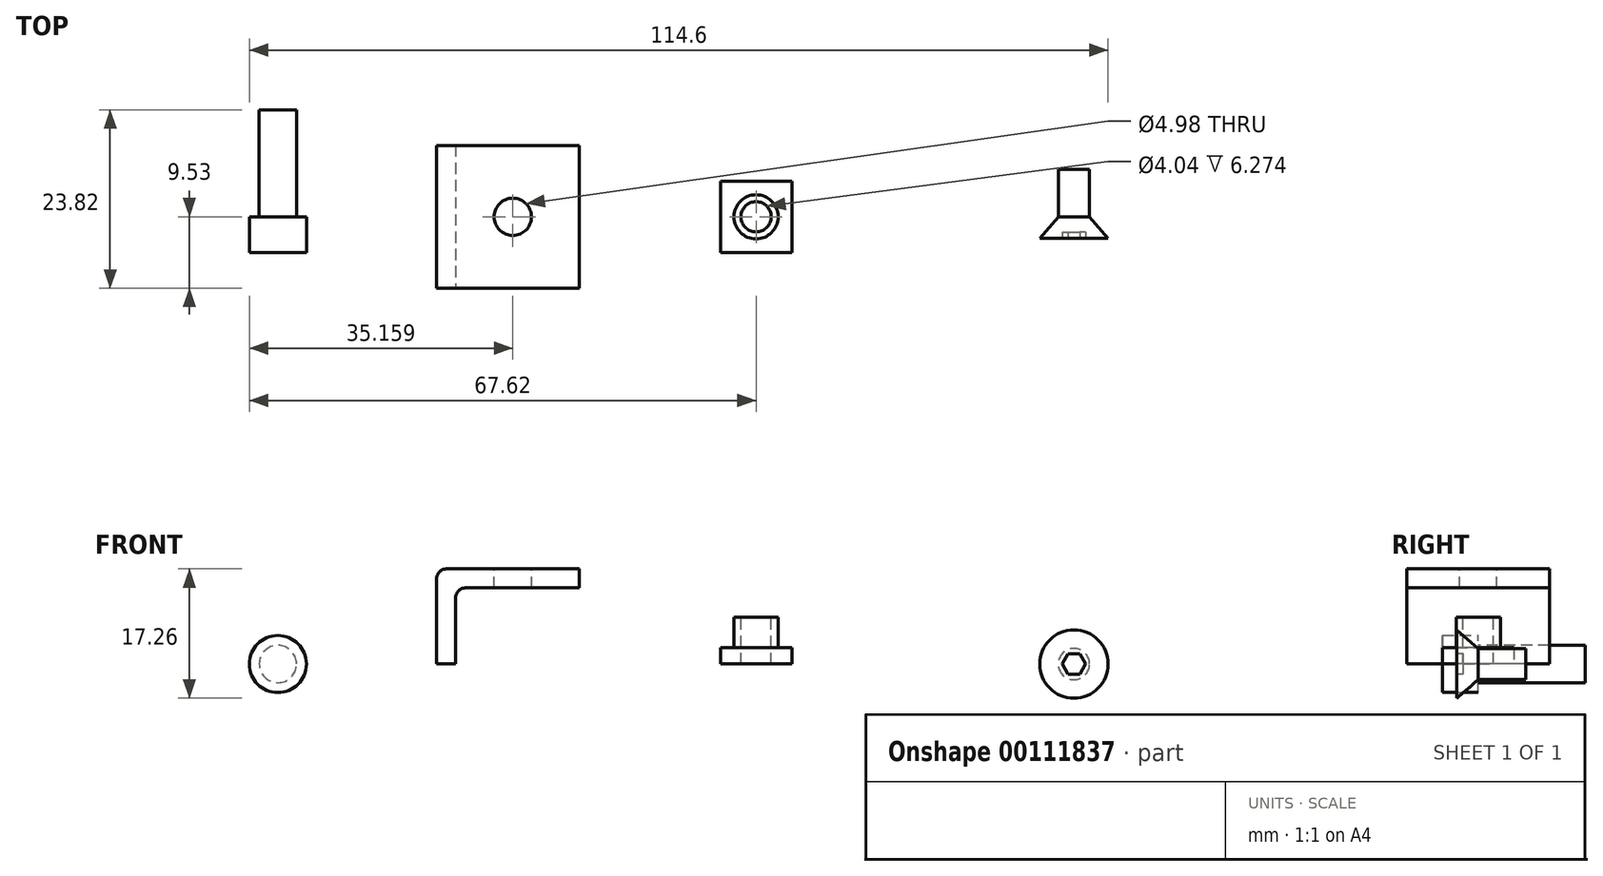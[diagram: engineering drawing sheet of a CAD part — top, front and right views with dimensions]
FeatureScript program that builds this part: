
annotation { "Feature Type Name" : "Feature", "Feature Type Description" : "" }
export const myFeature = defineFeature(function(context is Context, id is Id, definition is map)
    precondition{}
    {
        {
            var Q0;
            Q0=qCreatedBy(makeId("Top.planeOp"),FACE);
            var sketch = newSketch(context, id + "F0", { "sketchPlane" : qUnion([Q0])});
            skLineSegment(sketch, "E0.bottom", {"start": v(4.76, 4.76) * mm, "end": v(-4.76, 4.76) * mm});
            skLineSegment(sketch, "E0.top", {"start": v(4.76, -4.76) * mm, "end": v(-4.76, -4.76) * mm});
            skLineSegment(sketch, "E0.left", {"start": v(4.76, 4.76) * mm, "end": v(4.76, -4.76) * mm});
            skLineSegment(sketch, "E0.right", {"start": v(-4.76, 4.76) * mm, "end": v(-4.76, -4.76) * mm});
            skPoint(sketch, "E0.middle", {"position": v(0, 0) * mm});
            skSolve(sketch);
        }
        {
            var Q0;
            Q0=qSketchRegion(id+"F0",true);
            extrude(context, id + "F1", {"entities" : qUnion([Q0]), "depth" : 2.2 * mm});
        }
        {
            var Q0;
            Q0=makeQuery(id+"F1.opExtrude","CAP_FACE",FACE,{"disambiguationData":[OSD([sQuery(id+"F0.wireOp",EDGE,"E0.bottom"),sQuery(id+"F0.wireOp",EDGE,"E0.top"),sQuery(id+"F0.wireOp",EDGE,"E0.left"),sQuery(id+"F0.wireOp",EDGE,"E0.right")])],"isStart":false});
            var sketch = newSketch(context, id + "F2", { "sketchPlane" : qUnion([Q0])});
            skCircle(sketch, "E1", {"center": v(0, 0) * mm, "radius": 2.95 * mm});
            skSolve(sketch);
        }
        {
            var Q0;
            Q0=qSketchRegion(id+"F2",true);
            extrude(context, id + "F3", {"entities" : qUnion([Q0]), "operationType" : NewBodyOperationType.ADD, "depth" : 4.06 * mm});
        }
        {
            var Q0;
            Q0=makeQuery(id+"F3.opExtrude","CAP_FACE",FACE,{"disambiguationData":[OSD([sQuery(id+"F2.wireOp",EDGE,"E1")])],"isStart":false});
            var sketch = newSketch(context, id + "F4", { "sketchPlane" : qUnion([Q0])});
            skPoint(sketch, "E2", {"position": v(0, 0) * mm});
            skSolve(sketch);
        }
        {
            var Q0;
            Q0=sQuery(id+"F4.wireOp",VERTEX,"E2");
            var Q1;
            Q1=makeQuery(id+"F1.opExtrude","SWEPT_BODY",BODY,{"disambiguationData":[OSD([sQuery(id+"F0.wireOp",EDGE,"E0.bottom"),sQuery(id+"F0.wireOp",EDGE,"E0.top"),sQuery(id+"F0.wireOp",EDGE,"E0.left"),sQuery(id+"F0.wireOp",EDGE,"E0.right")])]});
            hole(context, id + "F5", {"style" : HoleStyle.SIMPLE, "holeDiameter" : 4.04 * mm, "endStyle" : HoleEndStyle.THROUGH, "locations" : qUnion([Q0]), "scope" : qUnion([Q1])});
        }
        {
            var Q0;
            Q0=qCreatedBy(makeId("Front.planeOp"),FACE);
            var sketch = newSketch(context, id + "F6", { "sketchPlane" : qUnion([Q0])});
            skLineSegment(sketch, "E3.bottom", {"start": v(-42.62, 0) * mm, "end": v(-23.57, 0) * mm});
            skLineSegment(sketch, "E3.top", {"start": v(-42.62, 12.7) * mm, "end": v(-23.57, 12.7) * mm});
            skLineSegment(sketch, "E3.left", {"start": v(-42.62, 0) * mm, "end": v(-42.62, 12.7) * mm});
            skLineSegment(sketch, "E3.right", {"start": v(-23.57, 0) * mm, "end": v(-23.57, 12.7) * mm});
            skSolve(sketch);
        }
        {
            var Q0;
            Q0=qSketchRegion(id+"F6",true);
            extrude(context, id + "F7", {"entities" : qUnion([Q0]), "depth" : 19.05 * mm, "symmetric" : true});
        }
        {
            var Q0;
            Q0=makeQuery(id+"F7.opExtrude","CAP_FACE",FACE,{"disambiguationData":[OSD([sQuery(id+"F6.wireOp",EDGE,"E3.bottom"),sQuery(id+"F6.wireOp",EDGE,"E3.top"),sQuery(id+"F6.wireOp",EDGE,"E3.left"),sQuery(id+"F6.wireOp",EDGE,"E3.right")])],"isStart":false});
            var sketch = newSketch(context, id + "F8", { "sketchPlane" : qUnion([Q0])});
            skLineSegment(sketch, "E4", {"start": v(-40.08, 0) * mm, "end": v(-40.08, 10.16) * mm});
            skLineSegment(sketch, "E5", {"start": v(-40.08, 10.16) * mm, "end": v(-23.57, 10.16) * mm});
            skLineSegment(sketch, "E6", {"start": v(-23.57, 10.16) * mm, "end": v(-23.57, 0) * mm});
            skLineSegment(sketch, "E7", {"start": v(-23.57, 0) * mm, "end": v(-40.08, 0) * mm});
            skSolve(sketch);
        }
        {
            var Q0;
            Q0=qSketchRegion(id+"F8",true);
            extrude(context, id + "F9", {"entities" : qUnion([Q0]), "operationType" : NewBodyOperationType.REMOVE, "endBound" : BoundingType.THROUGH_ALL, "oppositeDirection" : true, "depth" : 25.4 * mm});
        }
        {
            var Q0;
            Q0=makeQuery(id+"F7.opExtrude","SWEPT_EDGE",EDGE,{"disambiguationData":[OSD([sQuery(id+"F6.wireOp",EDGE,"E3.top"),sQuery(id+"F6.wireOp",EDGE,"E3.left")])]});
            var Q1;
            Q1=makeQuery(id+"F9.boolean.opBoolean","COPY",EDGE,{"derivedFrom":makeQuery(id+"F9.opExtrude","SWEPT_EDGE",EDGE,{"disambiguationData":[OSD([sQuery(id+"F8.wireOp",EDGE,"E4"),sQuery(id+"F8.wireOp",EDGE,"E5")])]})});
            fillet(context, id + "F10", {"entities" : qUnion([Q0, Q1]), "radius" : 1.27 * mm, "tangentPropagation" : true, "allowEdgeOverflow" : false});
        }
        {
            var Q0;
            Q0=makeQuery(id+"F7.opExtrude","SWEPT_FACE",FACE,{"disambiguationData":[OSD([sQuery(id+"F6.wireOp",EDGE,"E3.top")])]});
            var sketch = newSketch(context, id + "F11", { "sketchPlane" : qUnion([Q0])});
            skPoint(sketch, "E8", {"position": v(-32.46, 0) * mm});
            skLineSegment(sketch, "E9", {"start": v(-32.46, 9.52) * mm, "end": v(-32.46, 0) * mm, "construction": true});
            skLineSegment(sketch, "E10", {"start": v(-32.46, -9.52) * mm, "end": v(-32.46, 0) * mm, "construction": true});
            skLineSegment(sketch, "E11", {"start": v(-32.46, 0) * mm, "end": v(-23.57, 0) * mm, "construction": true});
            skLineSegment(sketch, "E12", {"start": v(-42.62, 0) * mm, "end": v(-32.46, 0) * mm, "construction": true});
            skSolve(sketch);
        }
        {
            var Q0;
            Q0=sQuery(id+"F11.wireOp",VERTEX,"E8");
            var Q1;
            Q1=makeQuery(id+"F7.opExtrude","SWEPT_BODY",BODY,{"disambiguationData":[OSD([sQuery(id+"F6.wireOp",EDGE,"E3.bottom"),sQuery(id+"F6.wireOp",EDGE,"E3.top"),sQuery(id+"F6.wireOp",EDGE,"E3.left"),sQuery(id+"F6.wireOp",EDGE,"E3.right")])]});
            hole(context, id + "F12", {"style" : HoleStyle.SIMPLE, "holeDiameter" : 4.98 * mm, "endStyle" : HoleEndStyle.THROUGH, "locations" : qUnion([Q0]), "scope" : qUnion([Q1])});
        }
        {
            var Q0;
            Q0=qCreatedBy(makeId("Front.planeOp"),FACE);
            var sketch = newSketch(context, id + "F13", { "sketchPlane" : qUnion([Q0])});
            skCircle(sketch, "E13", {"center": v(-63.81, 0) * mm, "radius": 3.81 * mm});
            skSolve(sketch);
        }
        {
            var Q0;
            Q0=makeQuery(id+"F13.imprint","IMPRINT",FACE,{"disambiguationData":[TD([[makeQuery(id+"F13.imprint","IMPRINT",EDGE,{"derivedFrom":sQuery(id+"F13.wireOp",EDGE,"E13")}),1.0]])]});
            extrude(context, id + "F14", {"entities" : qUnion([Q0]), "depth" : 4.76 * mm});
        }
        {
            var Q0;
            Q0=makeQuery(id+"F14.opExtrude","CAP_FACE",FACE,{"disambiguationData":[OSD([sQuery(id+"F13.wireOp",EDGE,"E13")])],"isStart":true});
            var sketch = newSketch(context, id + "F15", { "sketchPlane" : qUnion([Q0])});
            skCircle(sketch, "E14", {"center": v(63.81, 0) * mm, "radius": 2.49 * mm});
            skSolve(sketch);
        }
        {
            var Q0;
            Q0=qSketchRegion(id+"F15",true);
            extrude(context, id + "F16", {"entities" : qUnion([Q0]), "operationType" : NewBodyOperationType.ADD, "depth" : 14.29 * mm});
        }
        {
            var Q0;
            Q0=qCreatedBy(makeId("Front.planeOp"),FACE);
            var sketch = newSketch(context, id + "F17", { "sketchPlane" : qUnion([Q0])});
            skCircle(sketch, "E15", {"center": v(42.42, 0) * mm, "radius": 2.08 * mm});
            skSolve(sketch);
        }
        {
            var Q0;
            Q0=makeQuery(id+"F17.imprint","IMPRINT",FACE,{"disambiguationData":[TD([[makeQuery(id+"F17.imprint","IMPRINT",EDGE,{"derivedFrom":sQuery(id+"F17.wireOp",EDGE,"E15")}),1.0]])]});
            var Q1;
            Q1=sQuery(id+"F17.wireOp",EDGE,"D0WyXGXJ-a11A-hqUu-lPQ9-7sO1lFc8ZwJV");
            extrude(context, id + "F18", {"entities" : qUnion([Q0]), "surfaceEntities" : qUnion([Q1]), "depth" : 2.84 * mm, "hasDraft" : true, "draftAngle" : 41 * degree, "hasSecondDirection" : true, "secondDirectionOppositeDirection" : true, "secondDirectionDepth" : 6.35 * mm});
        }
        {
            var Q0;
            Q0=makeQuery(id+"F18.opExtrude","CAP_FACE",FACE,{"disambiguationData":[OSD([sQuery(id+"F17.wireOp",EDGE,"E15")])],"isStart":false});
            var sketch = newSketch(context, id + "F19", { "sketchPlane" : qUnion([Q0])});
            skCircle(sketch, "E16.cCircle", {"center": v(42.42, 0) * mm, "radius": 1.34 * mm, "construction": true});
            skLineSegment(sketch, "E16.0", {"start": v(43.97, 0) * mm, "end": v(43.2, -1.34) * mm});
            skLineSegment(sketch, "E16.1", {"start": v(43.2, -1.34) * mm, "end": v(41.65, -1.34) * mm});
            skLineSegment(sketch, "E16.2", {"start": v(41.65, -1.34) * mm, "end": v(40.87, 0) * mm});
            skLineSegment(sketch, "E16.3", {"start": v(40.87, 0) * mm, "end": v(41.65, 1.34) * mm});
            skLineSegment(sketch, "E16.4", {"start": v(41.65, 1.34) * mm, "end": v(43.2, 1.34) * mm});
            skLineSegment(sketch, "E16.5", {"start": v(43.2, 1.34) * mm, "end": v(43.97, 0) * mm});
            skPoint(sketch, "E16.0.midPoint", {"position": v(43.58, -0.67) * mm});
            skSolve(sketch);
        }
        {
            var Q0;
            Q0=makeQuery(id+"F19.imprint","IMPRINT",FACE,{"disambiguationData":[TD([[makeQuery(id+"F19.imprint","IMPRINT",EDGE,{"derivedFrom":sQuery(id+"F19.wireOp",EDGE,"E16.0")}),-1.0]])]});
            extrude(context, id + "F20", {"entities" : qUnion([Q0]), "operationType" : NewBodyOperationType.REMOVE, "oppositeDirection" : true, "depth" : 0.8 * mm});
        }
    });
